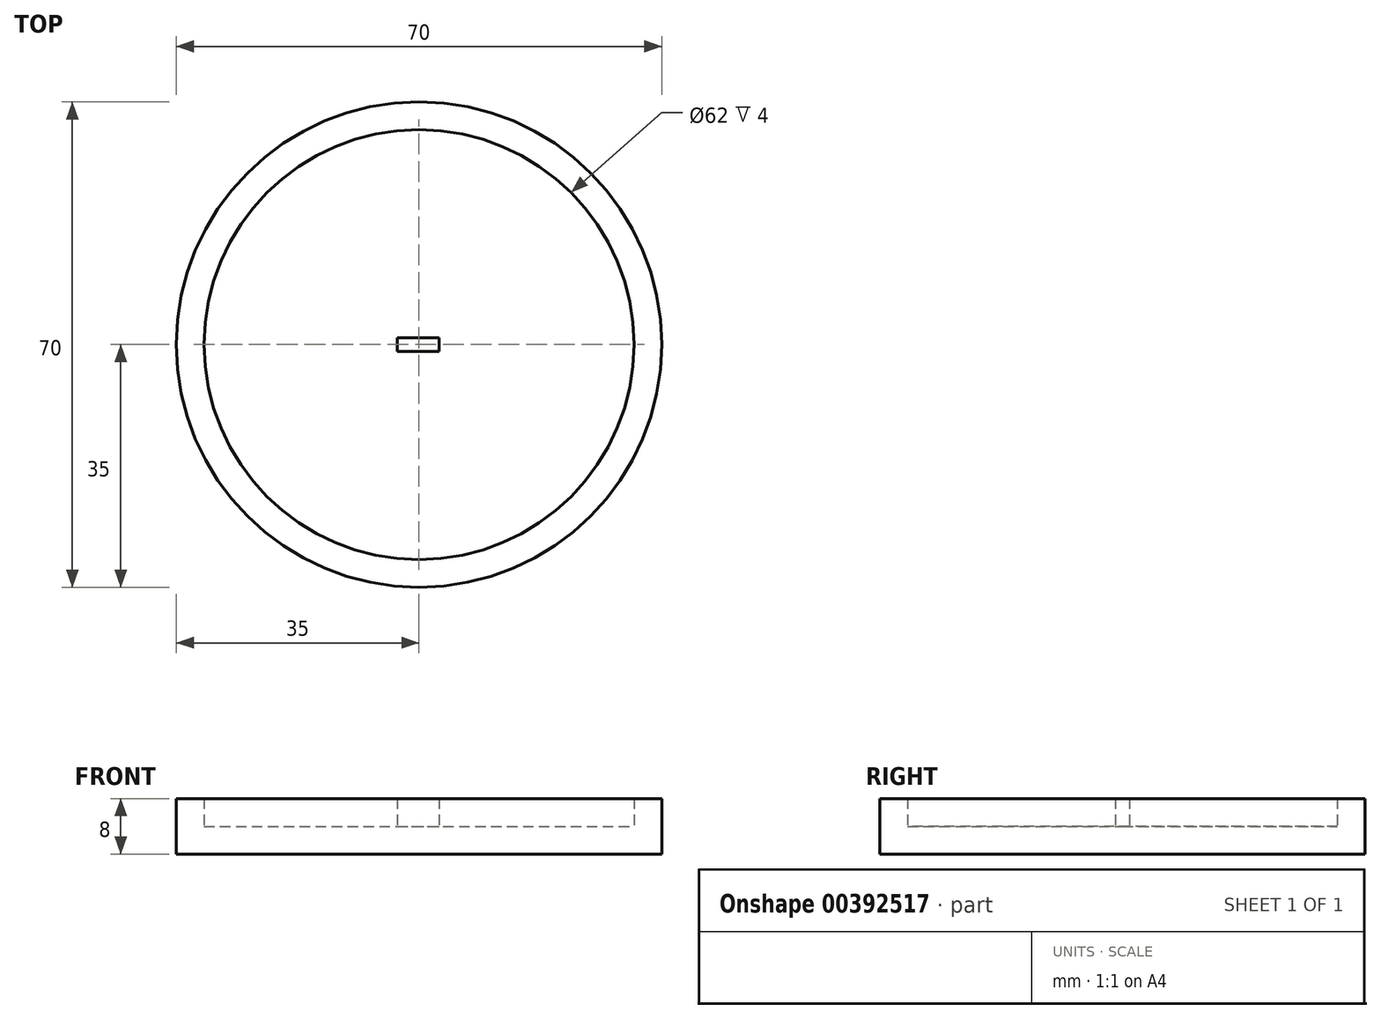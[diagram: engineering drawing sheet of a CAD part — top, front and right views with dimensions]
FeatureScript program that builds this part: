
annotation { "Feature Type Name" : "Feature", "Feature Type Description" : "" }
export const myFeature = defineFeature(function(context is Context, id is Id, definition is map)
    precondition{}
    {
        {
            var Q0;
            Q0=qCreatedBy(makeId("Front.planeOp"),FACE);
            var sketch = newSketch(context, id + "F0", { "sketchPlane" : qUnion([Q0])});
            skLineSegment(sketch, "E0", {"start": v(0, 0) * mm, "end": v(31, 0) * mm});
            skLineSegment(sketch, "E1", {"start": v(31, 0) * mm, "end": v(31, 4) * mm});
            skLineSegment(sketch, "E2", {"start": v(31, 4) * mm, "end": v(35, 4) * mm});
            skLineSegment(sketch, "E3", {"start": v(35, 4) * mm, "end": v(35, -4) * mm});
            skLineSegment(sketch, "E4", {"start": v(35, -4) * mm, "end": v(0, -4) * mm});
            skLineSegment(sketch, "E5", {"start": v(0, -4) * mm, "end": v(0, 0) * mm});
            skSolve(sketch);
        }
        {
            var Q0;
            Q0 = qSketchRegion(id + "F0", true);
            var Q1;
            Q1=sQuery(id+"F0.wireOp",EDGE,"E5");
            revolve(context, id + "F1", {"entities" : qUnion([Q0]), "axis" : qUnion([Q1]), "revolveType" : RevolveType.FULL});
        }
        {
            var Q0;
            Q0=makeQuery(id+"F1.opRevolve","SWEPT_FACE",FACE,{"disambiguationData":[OSD([sQuery(id+"F0.wireOp",EDGE,"E0")])]});
            var sketch = newSketch(context, id + "F2", { "sketchPlane" : qUnion([Q0])});
            skLineSegment(sketch, "E6.bottom", {"start": v(-3.13, 1) * mm, "end": v(2.87, 1) * mm});
            skLineSegment(sketch, "E6.top", {"start": v(-3.13, -1) * mm, "end": v(2.87, -1) * mm});
            skLineSegment(sketch, "E6.left", {"start": v(-3.13, 1) * mm, "end": v(-3.13, -1) * mm});
            skLineSegment(sketch, "E6.right", {"start": v(2.87, 1) * mm, "end": v(2.87, -1) * mm});
            skLineSegment(sketch, "E7", {"start": v(-0.13, 1) * mm, "end": v(-0.13, 31) * mm});
            skSolve(sketch);
        }
        {
            var Q0;
            Q0=makeQuery(id+"F2.imprint","IMPRINT",FACE,{"disambiguationData":[TD([[makeQuery(id+"F2.imprint","IMPRINT",EDGE,{"derivedFrom":sQuery(id+"F2.wireOp",EDGE,"E6.top")}),1.0]])]});
            var Q1;
            Q1=sQuery(id+"F2.wireOp",EDGE,"E6.right");
            var Q2;
            Q2=sQuery(id+"F2.wireOp",EDGE,"E6.left");
            var Q3;
            Q3=sQuery(id+"F2.wireOp",EDGE,"E6.bottom");
            var Q4;
            Q4=sQuery(id+"F2.wireOp",EDGE,"E6.top");
            extrude(context, id + "F3", {"entities" : qUnion([Q0]), "surfaceEntities" : qUnion([Q1, Q2, Q3, Q4]), "depth" : 4 * mm});
        }
    });
